# Revit family: LUMINOUS NEON DUAL 1217_NF1217.SW.1
name_source: partatom
category: Luminarias
units: mm (PartAtom-declared; Revit-internal decimal feet)

## family parameters
Compartido = No
Corte con vacíos al cargar = No
Cota de conector redondo = Diámetro de uso
Origen de luz = Sí
Punto de cálculo de habitación = No
Se basa en plano de trabajo = Sí
Siempre vertical = No
Tipo de pieza = Normal

## types (1)
- LUMINOUS NEON DUAL 1217_NF1217.SW.1
    Archivo de red fotométrica = NF1217W_LUMINOUS NEON .IES
    Cambio de temperatura de color de luz atenuada = <Ninguno>
    Comentarios de vataje = 24
    Descripción = TIRA LED LUMINOUS NEON DUAL 1217  DE SILICONA AMBIENTAL CON UNA POTENCIA DE 14W/M, USO PARA EXTERIORES IP67, IRC 80, IK 08, TEMPERATURA DUAL DE BLANCO CALIDO 2300-4000K, 650 LUMENES/M, PRESENTACION DE 5M, CORTE 10CM, ALIMENTADO A 24V, REQUIERE ACCESORIOS. RESISTENTE CONTRA SOLUCIONES SALINAS, ACIDOS ALCALINOS Y CONTRA GASES CORROSIVOS ADEMAS DE RAYOS UV.
    Elevación por defecto = 0 mm  [stored 0 ft]
    Fabricante = BRILLANT
    Filtro de color = 16777215
    Longitud de línea de emisión = 600 mm
    Marca = BRILLANT
    Modelo = NF1217.SW.1
    Modelo Lampara = 2835 SMD
    Ángulo de inclinación = 60.00°

note: [stored X ft] marks values corroborated as IEEE doubles in the binary element streams (Revit-internal decimal feet)

## geometry (parser evidence)
native form markers: Blend x2
no freeform markers — native parametric forms only
